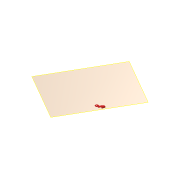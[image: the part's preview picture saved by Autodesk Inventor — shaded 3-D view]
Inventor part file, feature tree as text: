
AUTODESK INVENTOR PART (.ipt)
format: ipt  version: 2016 (Build 200138000, 138)  size: 398,336 bytes
history: native  units: mm
features: sheet_metal_op x13, reference x9, sketch x7, other x6, fillet x5, extrude x2, projected_geometry x2, plane x1
ambient origin geometry x8: Origin, YZ Plane, XZ Plane, XY Plane, X Axis, Y Axis, Z Axis, Center Point
bodies: Solid1 (feature_tree)
feature tree (45):
  plane  "Work Plane1"
  sheet_metal_op  "Face1"
  extrude  "Extrusion1"  Depth=0.75mm
  fillet  "Fillet1"  Radius=1.0mm
  fillet  "Fillet2"  Radius=3.0mm
  fillet  "Fillet3"  Radius=15.0mm
  sheet_metal_op  "Flange1"
  sheet_metal_op  "Flange2"
  sheet_metal_op  "Flange3"
  extrude  "Extrusion2"  Depth=0.5mm TaperAngle=0.0deg
  fillet  "Fillet4"  Radius=8.0mm
  sheet_metal_op  "Flange4"
  fillet  "Fillet5"  Radius=3.0mm
  sketch  "Sketch1"  dims[d0=16.0mm d3=0.75mm d4=1.0mm d5=3.0mm d7=15.0mm]
  reference  "Reference9"
  reference  "Reference10"
  reference  "Reference11"
  reference  "Reference12"
  reference  "Reference13"
  reference  "Reference14"
  reference  "Reference15"
  reference  "Reference16"
  other  "Plate1"
  sketch  "Sketch2"  dims[d8=2.0mm d9=1.0mm d10=0.5mm d11=0.0mm d12=8.0mm d13=3.0mm]
  projected_geometry  "Projected Loop1"
  reference  "Reference17"
  sketch  "Sketch3"  dims[d14=1.0mm]
  other  "Plate2"
  sheet_metal_op  "Bend1"
  sheet_metal_op  "Corner1"
  sketch  "Sketch4"  dims[d15=2.0mm]
  other  "Plate3"
  sheet_metal_op  "Bend2"
  sheet_metal_op  "Corner2"
  sketch  "Sketch5"  dims[d16=7.0mm]
  other  "Plate4"
  sheet_metal_op  "Bend3"
  sheet_metal_op  "Corner3"
  sketch  "Sketch6"  dims[d17=21.0mm]
  projected_geometry  "Projected Loop2"
  sketch  "Sketch7"  dims[d18=0.5mm d19=0.25mm d20=1.0mm d21=0.75mm d22=3.8mm d23=20.071286mm d24=0.75mm d25=2.0mm d26=0.5mm d27=0.75mm d28=0.5mm d29=0.25mm d30=1.0mm d31=0.75mm d32=3.2mm d33=6.981317mm d34=0.75mm d35=2.0mm d36=0.5mm d37=0.75mm d38=0.5mm d39=0.25mm d40=1.0mm d41=0.75mm d42=7.5mm d43=22.68928mm d44=0.75mm d45=2.0mm d46=0.5mm d47=0.75mm d48=0.5mm d49=0.0mm d50=4.0mm d51=2.0mm d52=0.5mm d53=0.25mm d54=1.0mm d55=0.75mm d56=3.0mm d57=75.0deg d58=0.75mm d59=2.0mm d60=0.5mm d61=0.75mm d1=10.0mm d2=4.7mm d6=1.0mm]
  other  "Plate5"
  sheet_metal_op  "Bend4"
  sheet_metal_op  "Corner4"
  other  "Definition1"
